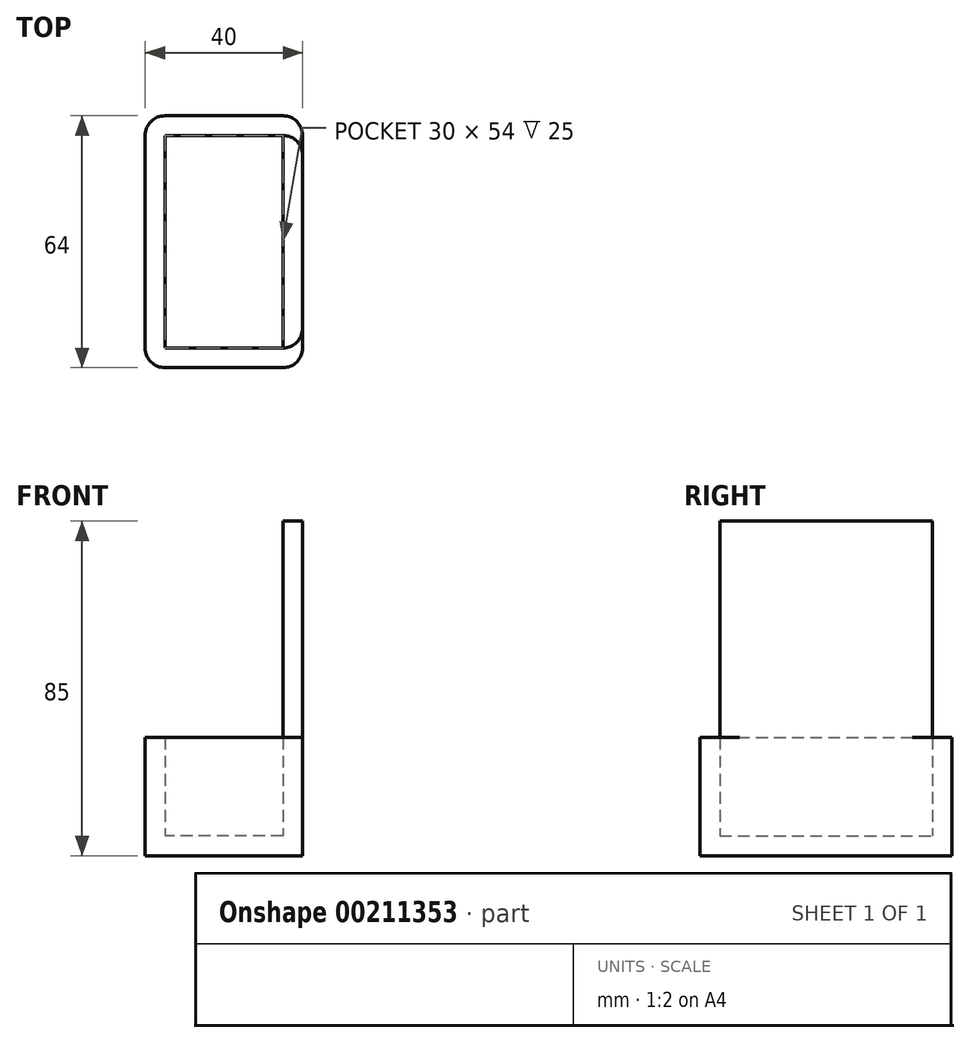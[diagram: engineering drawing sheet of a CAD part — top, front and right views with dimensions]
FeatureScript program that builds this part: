
annotation { "Feature Type Name" : "Feature", "Feature Type Description" : "" }
export const myFeature = defineFeature(function(context is Context, id is Id, definition is map)
    precondition{}
    {
        {
            var Q0;
            Q0=qCreatedBy(makeId("Top.planeOp"),FACE);
            var sketch = newSketch(context, id + "F0", { "sketchPlane" : qUnion([Q0])});
            skLineSegment(sketch, "E0.bottom", {"start": v(15, -27) * mm, "end": v(-15, -27) * mm});
            skLineSegment(sketch, "E0.top", {"start": v(15, 27) * mm, "end": v(-15, 27) * mm});
            skLineSegment(sketch, "E0.left", {"start": v(15, -27) * mm, "end": v(15, 27) * mm});
            skLineSegment(sketch, "E0.right", {"start": v(-15, -27) * mm, "end": v(-15, 27) * mm});
            skPoint(sketch, "E0.middle", {"position": v(0, 0) * mm});
            skLineSegment(sketch, "E1.0", {"start": v(-20, -31.96) * mm, "end": v(-20, 32.07) * mm});
            skLineSegment(sketch, "E2.0", {"start": v(20, 32) * mm, "end": v(-20.07, 32) * mm});
            skLineSegment(sketch, "E2.1", {"start": v(20, -32) * mm, "end": v(20, 32) * mm});
            skLineSegment(sketch, "E2.2", {"start": v(20, -32) * mm, "end": v(-20, -32) * mm});
            skLineSegment(sketch, "E3", {"start": v(-20.07, 32) * mm, "end": v(-20, 32.07) * mm});
            skLineSegment(sketch, "E4", {"start": v(-20, -31.96) * mm, "end": v(-20, -32) * mm});
            skLineSegment(sketch, "E5", {"start": v(15, 27) * mm, "end": v(20, 27) * mm});
            skLineSegment(sketch, "E6", {"start": v(15, -27) * mm, "end": v(20, -27) * mm});
            skLineSegment(sketch, "E7.bottom", {"start": v(20, 35.13) * mm, "end": v(43, 35.13) * mm});
            skLineSegment(sketch, "E7.top", {"start": v(20, -34.87) * mm, "end": v(43, -34.87) * mm});
            skLineSegment(sketch, "E7.left", {"start": v(20, 35.13) * mm, "end": v(20, -34.87) * mm});
            skLineSegment(sketch, "E7.right", {"start": v(43, 35.13) * mm, "end": v(43, -34.87) * mm});
            skSolve(sketch);
        }
        {
            var Q0;
            Q0=makeQuery(id+"F0.imprint","IMPRINT",FACE,{"disambiguationData":[TD([[makeQuery(id+"F0.imprint","IMPRINT",EDGE,{"derivedFrom":sQuery(id+"F0.wireOp",EDGE,"E0.left")}),-1.0]])]});
            extrude(context, id + "F1", {"entities" : qUnion([Q0]), "depth" : 85 * mm});
        }
        {
            var Q0;
            Q0=makeQuery(id+"F0.imprint","IMPRINT",FACE,{"disambiguationData":[TD([[makeQuery(id+"F0.imprint","IMPRINT",EDGE,{"derivedFrom":sQuery(id+"F0.wireOp",EDGE,"E0.bottom")}),-1.0]])]});
            extrude(context, id + "F2", {"entities" : qUnion([Q0]), "operationType" : NewBodyOperationType.ADD, "depth" : 5 * mm});
        }
        {
            var Q0;
            Q0=makeQuery(id+"F0.imprint","IMPRINT",FACE,{"disambiguationData":[TD([[makeQuery(id+"F0.imprint","IMPRINT",EDGE,{"derivedFrom":sQuery(id+"F0.wireOp",EDGE,"E0.bottom")}),1.0]])]});
            extrude(context, id + "F3", {"entities" : qUnion([Q0]), "operationType" : NewBodyOperationType.ADD, "depth" : 30 * mm});
        }
        {
            var Q0;
            Q0=makeQuery(id+"F3.opExtrude","SWEPT_EDGE",EDGE,{"disambiguationData":[OSD([sQuery(id+"F0.wireOp",EDGE,"E2.2"),sQuery(id+"F0.wireOp",EDGE,"E4")])]});
            var Q1;
            Q1=makeQuery(id+"F3.opExtrude","SWEPT_EDGE",EDGE,{"disambiguationData":[OSD([sQuery(id+"F0.wireOp",EDGE,"E2.1"),sQuery(id+"F0.wireOp",EDGE,"E2.2")])]});
            var Q2;
            Q2=makeQuery(id+"F3.opExtrude","SWEPT_EDGE",EDGE,{"disambiguationData":[OSD([sQuery(id+"F0.wireOp",EDGE,"E2.0"),sQuery(id+"F0.wireOp",EDGE,"E2.1")])]});
            var Q3;
            Q3=makeQuery(id+"F3.opExtrude","SWEPT_EDGE",EDGE,{"disambiguationData":[OSD([sQuery(id+"F0.wireOp",EDGE,"E1.0"),sQuery(id+"F0.wireOp",EDGE,"E2.0")])]});
            var Q4;
            Q4=makeQuery(id+"F1.opExtrude","SWEPT_EDGE",EDGE,{"disambiguationData":[OSD([sQuery(id+"F0.wireOp",EDGE,"E2.1"),sQuery(id+"F0.wireOp",EDGE,"E5")])]});
            var Q5;
            Q5=makeQuery(id+"F1.opExtrude","SWEPT_EDGE",EDGE,{"disambiguationData":[OSD([sQuery(id+"F0.wireOp",EDGE,"E2.1"),sQuery(id+"F0.wireOp",EDGE,"E6")])]});
            fillet(context, id + "F4", {"entities" : qUnion([Q0, Q1, Q2, Q3, Q4, Q5]), "radius" : 5 * mm, "tangentPropagation" : true, "allowEdgeOverflow" : false});
        }
    });
